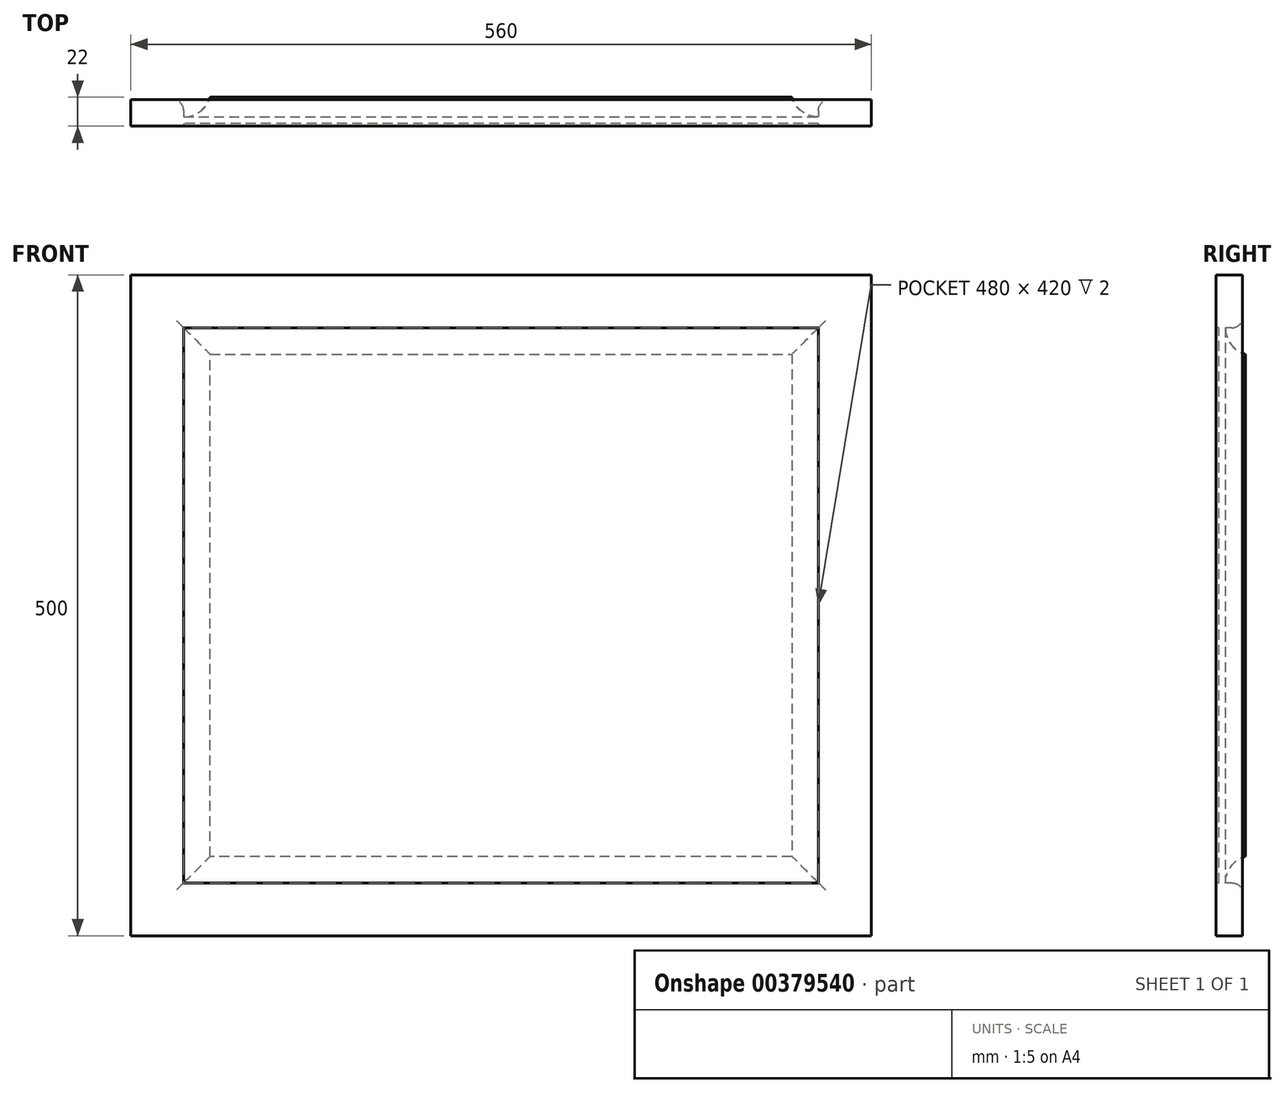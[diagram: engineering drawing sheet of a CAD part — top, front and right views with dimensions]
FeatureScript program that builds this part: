
annotation { "Feature Type Name" : "Feature", "Feature Type Description" : "" }
export const myFeature = defineFeature(function(context is Context, id is Id, definition is map)
    precondition{}
    {
        {
            var Q0;
            Q0=qCreatedBy(makeId("Front.planeOp"),FACE);
            var sketch = newSketch(context, id + "F0", { "sketchPlane" : qUnion([Q0])});
            skLineSegment(sketch, "E0.bottom", {"start": v(-280, 250) * mm, "end": v(280, 250) * mm});
            skLineSegment(sketch, "E0.top", {"start": v(-280, -250) * mm, "end": v(280, -250) * mm});
            skLineSegment(sketch, "E0.left", {"start": v(-280, 250) * mm, "end": v(-280, -250) * mm});
            skLineSegment(sketch, "E0.right", {"start": v(280, 250) * mm, "end": v(280, -250) * mm});
            skPoint(sketch, "E0.middle", {"position": v(0, 0) * mm});
            skLineSegment(sketch, "E1", {"start": v(-280, 250) * mm, "end": v(-93.33, 250) * mm, "construction": true});
            skLineSegment(sketch, "E2", {"start": v(-93.33, 250) * mm, "end": v(93.33, 250) * mm, "construction": true});
            skLineSegment(sketch, "E3", {"start": v(93.33, 250) * mm, "end": v(280, 250) * mm, "construction": true});
            skLineSegment(sketch, "E4", {"start": v(-93.33, 250) * mm, "end": v(-93.33, -250) * mm});
            skLineSegment(sketch, "E5", {"start": v(93.33, 250) * mm, "end": v(93.33, -250) * mm});
            skSolve(sketch);
        }
        {
            var Q0;
            Q0=qCreatedBy(makeId("Top.planeOp"),FACE);
            var sketch = newSketch(context, id + "F1", { "sketchPlane" : qUnion([Q0])});
            skLineSegment(sketch, "E6", {"start": v(0, 0) * mm, "end": v(-280, 0) * mm, "construction": true});
            skLineSegment(sketch, "E7", {"start": v(0, 0) * mm, "end": v(280, 0) * mm});
            skLineSegment(sketch, "E8", {"start": v(-280, 0) * mm, "end": v(-280, -7) * mm});
            skLineSegment(sketch, "E9", {"start": v(-280, -7) * mm, "end": v(-240, -7) * mm});
            skLineSegment(sketch, "E10", {"start": v(-240, -7) * mm, "end": v(-240, 0) * mm});
            skLineSegment(sketch, "E11", {"start": v(-240, 0) * mm, "end": v(-220, 0) * mm});
            skLineSegment(sketch, "E12", {"start": v(-220, 0) * mm, "end": v(-220, 15) * mm});
            skLineSegment(sketch, "E13", {"start": v(-280, 0) * mm, "end": v(-30, 0) * mm, "construction": true});
            skLineSegment(sketch, "E14", {"start": v(-220, 15) * mm, "end": v(-30, 15) * mm});
            skLineSegment(sketch, "E15", {"start": v(-30, 15) * mm, "end": v(-30, 0) * mm});
            skArc(sketch, "E16", {"start": v(-240, 0) * mm, "mid": v(-227.5, 4.17) * mm, "end": v(-220, 15) * mm});
            skLineSegment(sketch, "E17", {"start": v(-280, 0) * mm, "end": v(-280, 13) * mm});
            skLineSegment(sketch, "E18", {"start": v(-240, 0) * mm, "end": v(-240, 5) * mm});
            skArc(sketch, "E19", {"start": v(-240, 5) * mm, "mid": v(-242.34, 10.66) * mm, "end": v(-248, 13) * mm});
            skLineSegment(sketch, "E20", {"start": v(-240, -5) * mm, "end": v(-30, -5) * mm});
            skLineSegment(sketch, "E21", {"start": v(-30, -5) * mm, "end": v(-30, 0) * mm});
            skLineSegment(sketch, "E22", {"start": v(-280, 13) * mm, "end": v(-248, 13) * mm});
            skSolve(sketch);
        }
        {
            var Q0;
            {var subQ0=sQuery(id+"F1.wireOp",EDGE,"E11");Q0=makeQuery(id+"F1.imprint","IMPRINT",FACE,{"disambiguationData":[TD([[makeQuery(id+"F1.imprint","IMPRINT",EDGE,{"derivedFrom":subQ0}),-1.0]])]});}
            var Q1;
            Q1=makeQuery(id+"F1.imprint","IMPRINT",FACE,{"disambiguationData":[TD([[makeQuery(id+"F1.imprint","IMPRINT",EDGE,{"derivedFrom":sQuery(id+"F1.wireOp",EDGE,"E11")}),1.0]])]});
            var Q2;
            Q2=makeQuery(id+"F1.imprint","IMPRINT",FACE,{"disambiguationData":[TD([[makeQuery(id+"F1.imprint","IMPRINT",EDGE,{"derivedFrom":sQuery(id+"F1.wireOp",EDGE,"E8")}),1.0]])]});
            var Q3;
            Q3=sQuery(id+"F0.wireOp",EDGE,"E0.left");
            var Q4;
            Q4=sQuery(id+"F0.wireOp",EDGE,"E0.bottom");
            var Q5;
            Q5=sQuery(id+"F0.wireOp",EDGE,"E0.right");
            var Q6;
            Q6=sQuery(id+"F0.wireOp",EDGE,"E0.top");
            sweep(context, id + "F2", {"profiles" : qUnion([Q0, Q1, Q2]), "path" : qUnion([Q3, Q4, Q5, Q6])});
        }
    });
